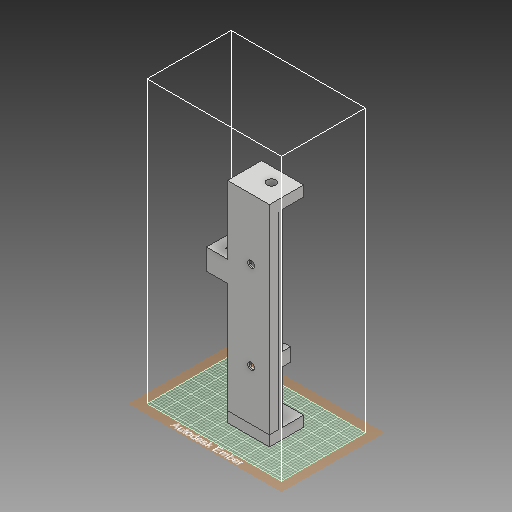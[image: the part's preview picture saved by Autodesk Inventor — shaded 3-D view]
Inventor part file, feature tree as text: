
AUTODESK INVENTOR PART (.ipt)
format: ipt  version: 2018 (Build 220112000, 112)  size: 612,864 bytes
history: native  units: mm
features: sketch x40, extrude x27, hole x8, fillet x5
ambient origin geometry x8: Origin, YZ Plane, XZ Plane, XY Plane, X Axis, Y Axis, Z Axis, Center Point
bodies: Solid1 (feature_tree)
feature tree (80):
  extrude  "Extrusion1"  Depth=100.0mm
  extrude  "Extrusion2"  Depth=5.0mm
  sketch  "Sketch3"  dims[d5=5.0mm d6=40.0mm d7=0.0mm]
  hole  "Hole1"  [1 undecoded]
  extrude  "Extrusion3"  Depth=2.0mm
  hole  "Hole2"  [1 undecoded]
  fillet  "Fillet1"  Radius=8.5mm
  extrude  "Extrusion4"  TaperAngle=90.0deg  [1 undecoded]
  extrude  "Extrusion5"  TaperAngle=180.0deg  [1 undecoded]
  hole  "Hole3"  [1 undecoded]
  fillet  "Fillet2"  Radius=3.5mm
  extrude  "Extrusion6"  Depth=10.0mm
  extrude  "Extrusion7"  Depth=5.0mm TaperAngle=0.0deg
  extrude  "Extrusion8"  Depth=12.5mm TaperAngle=0.0deg
  extrude  "Extrusion9"  Depth=0.1mm
  hole  "Hole4"  [1 undecoded]
  extrude  "Extrusion10"  Depth=5.5mm
  hole  "Hole5"  [1 undecoded]
  extrude  "Extrusion11"  Depth=2.1mm TaperAngle=0.0deg
  extrude  "Extrusion12"  Depth=5.0mm
  extrude  "Extrusion13"  Depth=1.0mm TaperAngle=0.0deg
  extrude  "Extrusion14"  Depth=3.8mm TaperAngle=0.0deg
  sketch  "Sketch21"  dims[d66=6.35mm d67=3.8mm d68=0.0mm]
  extrude  "Extrusion15"  Depth=8.0mm TaperAngle=0.0deg
  sketch  "Sketch23"  dims[d78=3.3mm d79=6.0mm d80=4.0mm d81=2.0mm d82=90.0deg d83=80.0mm d84=20.594885mm d85=5.45mm]
  extrude  "Extrusion16"  Depth=2.0mm
  extrude  "Extrusion17"  Depth=10.5mm
  hole  "Hole6"  [1 undecoded]
  fillet  "Fillet3"  Radius=4.5mm
  extrude  "Extrusion18"  Depth=8.0mm TaperAngle=0.0deg
  sketch  "Sketch28"  dims[d100=4.1mm d101=0.0mm d102=5.0mm]
  extrude  "Extrusion19"  Depth=10.0mm
  extrude  "Extrusion20"  Depth=5.0mm
  extrude  "Extrusion21"  Depth=10.0mm TaperAngle=0.0deg
  hole  "Hole7"  [1 undecoded]
  extrude  "Extrusion22"  Depth=21.0mm
  extrude  "Extrusion23"  Depth=7.499983mm TaperAngle=0.0deg
  fillet  "Fillet4"  Radius=50.0mm
  fillet  "Fillet5"  Radius=7.499983mm
  extrude  "Extrusion24"  Depth=10.0mm
  extrude  "Extrusion25"  Depth=4.1mm TaperAngle=0.0deg
  hole  "Hole8"  [1 undecoded]
  extrude  "Extrusion26"  Depth=8.0mm TaperAngle=0.0deg
  sketch  "Sketch39"  dims[d142=3.85mm d143=0.0mm]
  extrude  "Extrusion27"  Depth=1.0mm
  sketch  "Sketch1"  dims[d0=22.65mm d1=100.0mm]
  sketch  "Sketch2"  dims[d2=5.0mm d3=0.0mm d4=5.0mm]
  sketch  "Sketch4"  dims[d8=10.0mm]
  sketch  "Sketch5"  dims[d9=4.0mm d10=6.0mm d11=4.0mm d12=2.0mm d13=90.0deg d14=115.0mm d15=20.594885mm d16=23.0mm]
  sketch  "Sketch6"  dims[d17=102.75mm d18=0.0mm d19=1.175mm d20=8.5mm]
  sketch  "Sketch7"  dims[d21=21.0mm d22=90.0deg]
  sketch  "Sketch8"  dims[d23=8.5mm d24=180.0deg]
  sketch  "Sketch9"  dims[d25=21.0mm]
  sketch  "Sketch10"  dims[d26=4.0mm d27=6.0mm d28=4.0mm d29=2.0mm d30=90.0deg d31=115.0mm d32=20.594885mm d33=1.0mm d34=3.5mm]
  sketch  "Sketch11"  dims[d35=15.825mm d36=10.0mm]
  sketch  "Sketch12"  dims[d37=10.0mm d38=5.0mm d39=0.0mm]
  sketch  "Sketch13"  dims[d40=5.0mm d41=12.5mm d42=0.0mm]
  sketch  "Sketch14"  dims[d43=6.0mm d44=6.0mm d45=4.0mm d46=2.0mm d47=90.0deg d48=115.0mm d49=20.594885mm d50=0.1mm]
  sketch  "Sketch15"  dims[d51=4.25mm d52=1000.0mm d53=0.0mm]
  sketch  "Sketch16"  dims[d54=3.3mm d55=5.5mm]
  sketch  "Sketch17"  dims[d56=3.2mm d57=3.0mm]
  sketch  "Sketch18"  dims[d58=2.1mm d59=91.25mm d60=0.0mm]
  sketch  "Sketch19"  dims[d61=4.44mm d62=5.0mm]
  sketch  "Sketch20"  dims[d63=1.0mm d64=91.25mm d65=0.0mm]
  sketch  "Sketch22"  dims[d69=3.3mm d70=6.0mm d71=4.0mm d72=2.0mm d73=90.0deg d74=8.0mm d75=20.594885mm d76=4.55mm d77=0.0mm]
  sketch  "Sketch24"  dims[d86=129.8mm d87=0.0mm d88=10.5mm]
  sketch  "Sketch25"  dims[d89=2.5mm d90=0.0mm d91=10.0mm d92=4.5mm d93=0.0mm]
  sketch  "Sketch26"  dims[d94=8.0mm d95=0.0mm d96=15.5mm d97=0.0mm]
  sketch  "Sketch27"  dims[d98=10.0mm d99=10.0mm]
  sketch  "Sketch29"  dims[d103=17.5mm d104=10.0mm d105=0.0mm]
  sketch  "Sketch30"  dims[d106=5.0mm]
  sketch  "Sketch31"  dims[d107=6.0mm d108=6.0mm d109=4.0mm d110=2.0mm d111=90.0deg d112=80.0mm d113=20.594885mm d114=2.0mm]
  sketch  "Sketch32"  dims[d115=45.0mm d116=0.0mm d117=21.0mm]
  sketch  "Sketch33"  dims[d118=4.5mm d119=118.0mm d120=0.0mm d121=50.0mm d122=7.499983mm]
  sketch  "Sketch34"  dims[d123=7.5mm d124=10.0mm]
  sketch  "Sketch35"  dims[d125=10.0mm d126=4.1mm d127=0.0mm]
  sketch  "Sketch36"  dims[d128=13.4mm d129=0.0mm d130=5.0mm]
  sketch  "Sketch37"  dims[d131=6.0mm d132=6.0mm d133=4.0mm d134=2.0mm d135=90.0deg d136=8.0mm d137=20.594885mm d138=130.4mm d139=0.0mm]
  sketch  "Sketch38"  dims[d140=1.0mm d141=1.0mm]
  sketch  "Sketch40"  dims[d144=3.0mm d145=2.0mm d146=100.0mm d147=0.0mm d148=4.0mm d149=10.0mm d150=5.0mm d151=15.0mm d152=7.5mm d153=7.5mm d154=0.0mm d155=6.0mm d156=6.0mm d157=4.0mm d158=2.0mm d159=90.0deg d160=8.0mm d161=20.594885mm d162=5.5mm d163=5.0mm d164=0.0mm d165=5.5mm d166=0.0mm]
note: 10 required parameter values undecoded (feature->parameter linkage not recoverable at this tier; creation-order binding heuristic only, values carry confidence <= 0.55)
